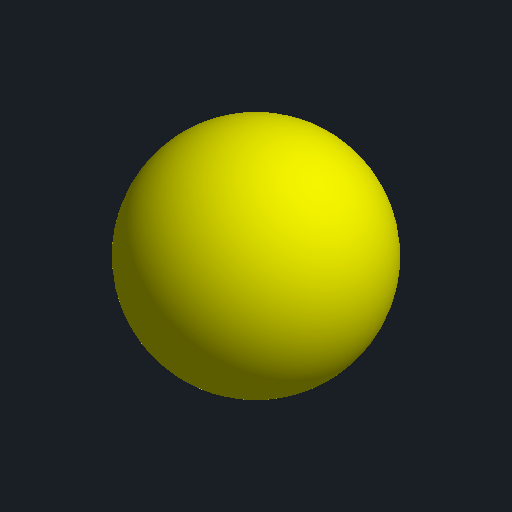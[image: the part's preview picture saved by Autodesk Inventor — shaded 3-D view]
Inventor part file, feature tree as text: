
AUTODESK INVENTOR PART (.ipt)
format: ipt  version: 2022 (Build 260153000, 153)  size: 117,760 bytes
history: native  units: mm (DEFAULTED — no unit token found)
features: revolve x1, sketch x1
ambient origin geometry x8: Origin, YZ Plane, XZ Plane, XY Plane, X Axis, Y Axis, Z Axis, Center Point
bodies: Solid1 (feature_tree)
feature tree (2):
  revolve  "Revolution1"  [1 undecoded]
  sketch  "Sketch_1"  dims[d0=360.0deg]
note: 1 required parameter value undecoded (feature->parameter linkage not recoverable at this tier; creation-order binding heuristic only, values carry confidence <= 0.55)
